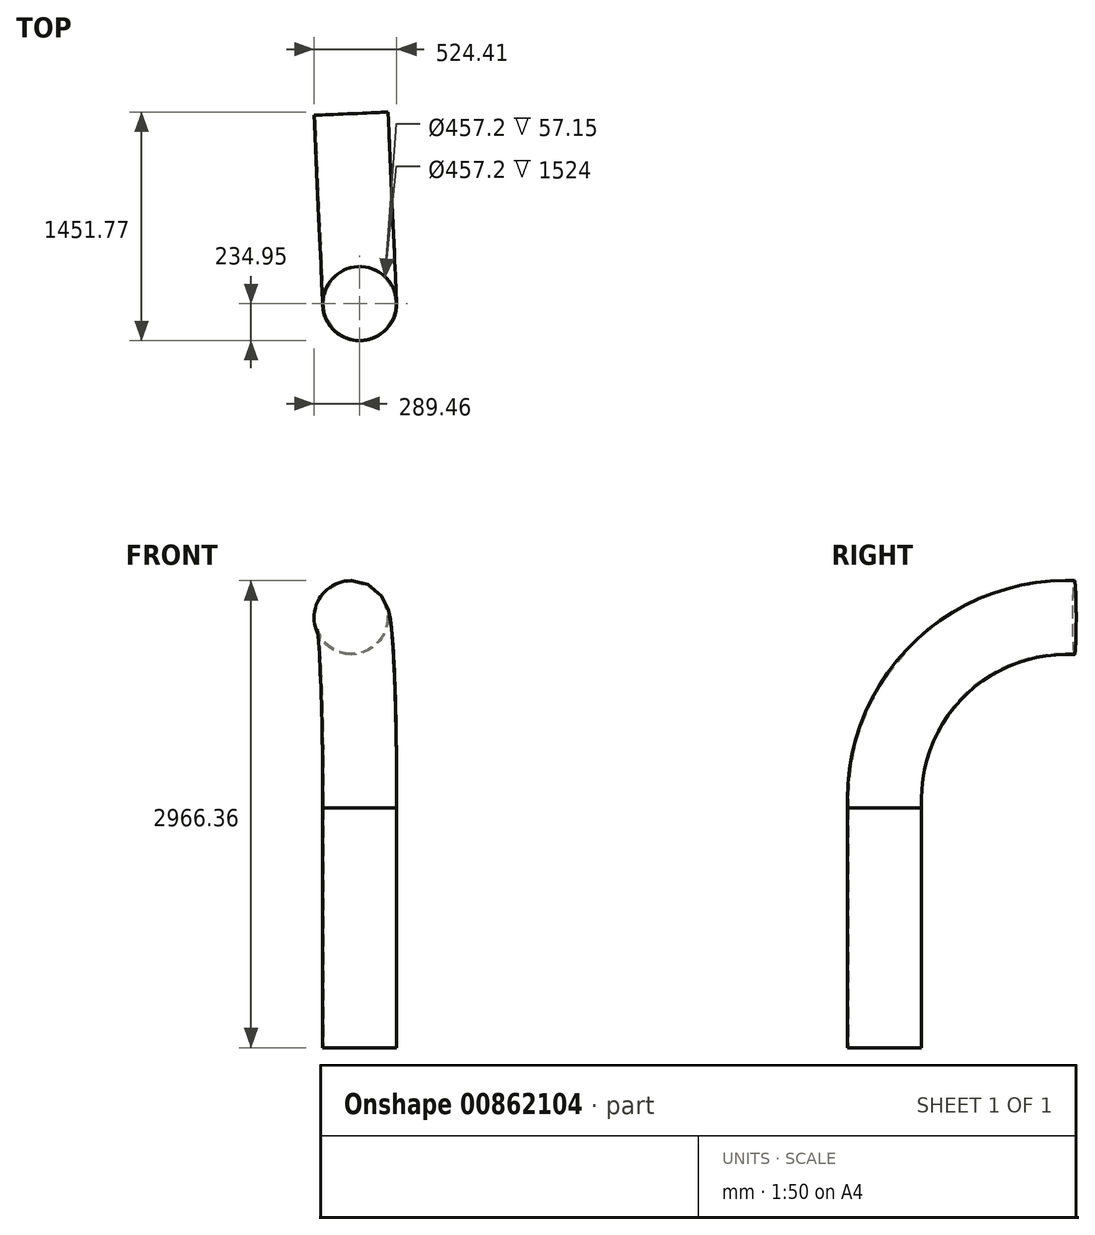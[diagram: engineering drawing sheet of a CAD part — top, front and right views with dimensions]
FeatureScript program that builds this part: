
annotation { "Feature Type Name" : "Feature", "Feature Type Description" : "" }
export const myFeature = defineFeature(function(context is Context, id is Id, definition is map)
    precondition{}
    {
        {
            var Q0;
            Q0=qCreatedBy(makeId("Top.planeOp"),FACE);
            var sketch = newSketch(context, id + "F0", { "sketchPlane" : qUnion([Q0])});
            skCircle(sketch, "E0", {"center": v(0, 0) * mm, "radius": 228.6 * mm});
            skCircle(sketch, "E1.0", {"center": v(0, 0) * mm, "radius": 234.95 * mm});
            skSolve(sketch);
        }
        {
            var Q0;
            Q0 = qSketchRegion(id + "F0", true);
            extrude(context, id + "F1", {"entities" : qUnion([Q0]), "depth" : 1524 * mm, "offsetDistance" : 25.4 * mm});
        }
        {
            var Q0;
            Q0=makeQuery(id+"F1.opExtrude","CAP_FACE",FACE,{"disambiguationData":[OSD([sQuery(id+"F0.wireOp",EDGE,"E0"),sQuery(id+"F0.wireOp",EDGE,"E1.0")])],"isStart":false});
            cPlane(context, id + "F2", {"entities" : qUnion([Q0]), "cplaneType" : CPlaneType.OFFSET, "offset" : 57.15 * mm, "width" : 152.4 * mm, "height" : 152.4 * mm});
        }
        {
            var Q0;
            Q0=qCreatedBy(id+"F2.planeOp",FACE);
            var sketch = newSketch(context, id + "F3", { "sketchPlane" : qUnion([Q0])});
            skLineSegment(sketch, "E2", {"start": v(0, 0) * mm, "end": v(0, 1143) * mm, "construction": true});
            skLineSegment(sketch, "E3", {"start": v(0, 1151.44) * mm, "end": v(-186, 1143) * mm});
            skSolve(sketch);
        }
        {
            var Q0;
            Q0=makeQuery(id+"F1.opExtrude","CAP_FACE",FACE,{"disambiguationData":[OSD([sQuery(id+"F0.wireOp",EDGE,"E0"),sQuery(id+"F0.wireOp",EDGE,"E1.0")])],"isStart":false});
            extrude(context, id + "F4", {"entities" : qUnion([Q0]), "depth" : 57.15 * mm, "offsetDistance" : 25.4 * mm});
        }
        {
            var Q0;
            Q0=makeQuery(id+"F4.opExtrude","CAP_FACE",FACE,{"disambiguationData":[OSD([sQuery(id+"F0.wireOp",EDGE,"E0"),sQuery(id+"F0.wireOp",EDGE,"E1.0")])],"isStart":false});
            var Q1;
            Q1=sQuery(id+"F3.wireOp",EDGE,"E3");
            revolve(context, id + "F5", {"operationType" : NewBodyOperationType.ADD, "surfaceOperationType" : NewSurfaceOperationType.NEW, "entities" : qUnion([Q0]), "axis" : qUnion([Q1]), "revolveType" : RevolveType.ONE_DIRECTION, "angle" : 90 * degree});
        }
        {
            var Q0;
            Q0=makeQuery(id+"F5.opRevolve","CAP_FACE",FACE,{"disambiguationData":[OSD([sQuery(id+"F0.wireOp",EDGE,"E0"),sQuery(id+"F0.wireOp",EDGE,"E1.0")])],"isStart":false});
            extrude(context, id + "F6", {"entities" : qUnion([Q0]), "operationType" : NewBodyOperationType.ADD, "depth" : 57.15 * mm, "offsetDistance" : 25.4 * mm});
        }
    });
